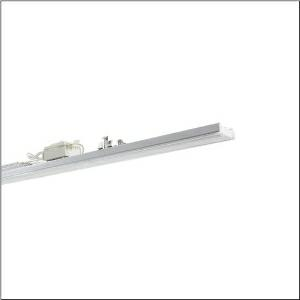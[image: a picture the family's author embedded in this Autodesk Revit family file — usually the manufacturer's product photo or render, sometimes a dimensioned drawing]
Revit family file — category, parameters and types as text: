
# Revit family: licross_21_recessed_mo_52tl147n48xg
name_source: partatom
category: Lighting Fixtures
units: mm (PartAtom-declared; Revit-internal decimal feet)

## family parameters
Cut with Voids When Loaded = No
Host = Face
Light Source = No
Part Type = Normal
Room Calculation Point = No
Round Connector Dimension = Use Diameter
Shared = No

## types (1)
- Licross 21 Recessed MO (1 x LED, 8120 lm, 47.9 W, 4000K)
    Apparent Load = 48 VA
    CIE Flux Codes = 56 84 97 100 100
    Color Rendering = 80
    Color Temperature = 4000K
    Default Elevation = 1800 mm
    Description = Licross 21 Recessed MO, luminaire insert, of sheet steel, galvanised, coil coated, white, length: 1.500mm, width: 66mm, height: 67mm, LED rated luminous flux: 8.120lm, light colour: 840, SDCM (Standard Deviation of Colour Matching)MacAdam ≤ 3 SDCM (initial), control gear: ON/OFF, with plug, 3-pole, with phase selection, mains connection: 220..240V, AC, 50/60Hz, rated input power: 48W, internal wiring halogen-free, primary light control with lens, of plastic, primary optical cover: cover, of PMMA, light emission: direct distribution, primary light characteristic: asymmetric, protection rating (complete): IP40, insulation class (complete): insulation class I (protective earthing), certification: CE, ENEC, VDE, UKCA, protection symbol: D if used in an environment without relevant dust loads with corresponding accessories, impact resistance: IK06, permissible ambient temperature for indoor applications: -35..+40°C, corresponds to IFS (International Featured Standards) requirements for safety and quality in the food industry, reducing of maximum allowable ambient temperature of 5°C with ceiling mounting, LABS conformity tested according to VDMA 24364:2018-05, The light source and the operating device comply with the requirements of the Ecodesign Regulation (EU) 2019/2020 and are replaceable in accordance with this regulation, packaging unit: 1 piece
    Height = 58 mm
    Lamp = 1 x LED
    Lamp Light Flux = 8120 lm
    Lamp Power = 47.9 W
    Lamp count = 1
    Length = 1500 mm
    Luminous efficacy = 170 lm/W
    Manufacturer = Siteco
    ModVariant = No
    Model = 52TL147N48XG
    Mounting Place = Ceiling
    Mounting Type = Pendant
    Number of Poles = 1
    OnlyDefault = Yes
    Power Factor = 1
    Product Name = Licross 21 Recessed MO
    Product group = luminaire insert | ceiling pendant
    ProductGroupID = 901
    Protection Class = Protection class I
    Protection Degree = IP 40
    RLX_Detail_Level = 1
    RLX_Emergency_Light_Flux = 0 lm
    RLX_Emergency_Type = 0
    RLX_Emergency_Type_DB = No
    RlxData = <blob elided: 21657 chars, md5=988d8592>
    Socket = socket
    Standby Power = 0 W
    System Light Flux = 8120 lm
    System Power = 48 W
    Type Comments = Product without accessories
    Type Image = l_1296930.jpg
    URL = http://relux.com
    VarID = ---
    Voltage = 0 V
    Weight = 0.00 kg
    Width = 66 mm

## geometry (parser evidence)
native form markers: Blend x4, Sweep x10
no freeform markers — native parametric forms only
